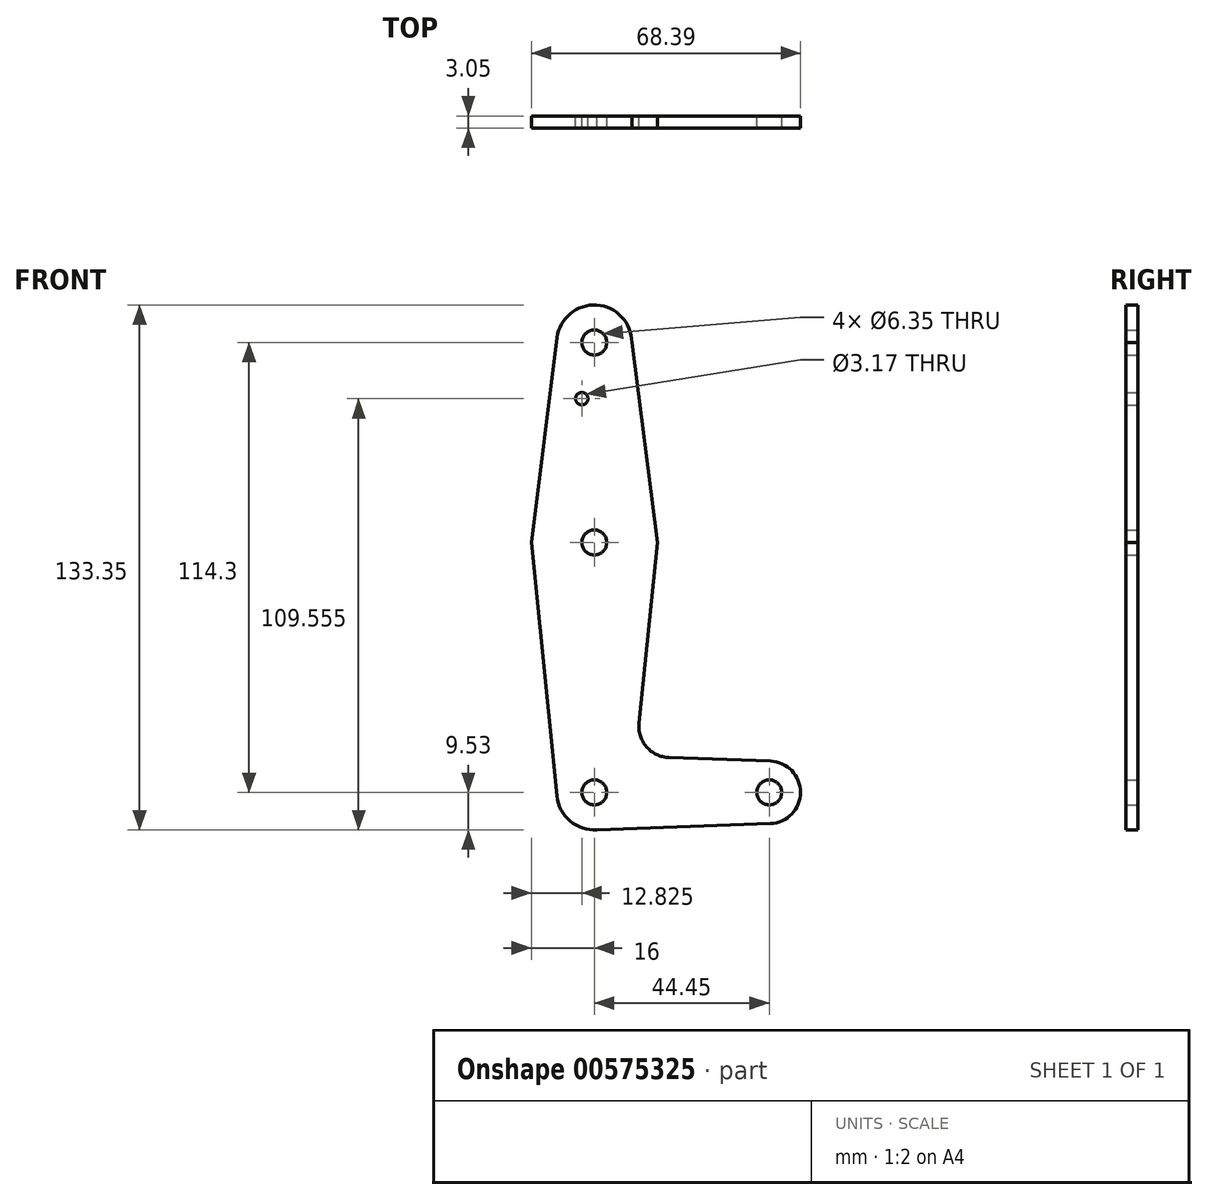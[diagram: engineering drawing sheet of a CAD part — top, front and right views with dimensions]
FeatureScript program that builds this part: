
annotation { "Feature Type Name" : "Feature", "Feature Type Description" : "" }
export const myFeature = defineFeature(function(context is Context, id is Id, definition is map)
    precondition{}
    {
        {
            var Q0;
            Q0=qCreatedBy(makeId("Front.planeOp"),FACE);
            var sketch = newSketch(context, id + "F0", { "sketchPlane" : qUnion([Q0])});
            skCircle(sketch, "E0", {"center": v(0, 0) * mm, "radius": 15.88 * mm});
            skLineSegment(sketch, "E1", {"start": v(0, 0) * mm, "end": v(0, -63.5) * mm, "construction": true});
            skCircle(sketch, "E2", {"center": v(0, -63.5) * mm, "radius": 9.53 * mm});
            skCircle(sketch, "E3", {"center": v(0, 50.8) * mm, "radius": 9.53 * mm});
            skLineSegment(sketch, "E4", {"start": v(0, -63.5) * mm, "end": v(44.45, -63.5) * mm, "construction": true});
            skCircle(sketch, "E5", {"center": v(44.45, -63.5) * mm, "radius": 7.94 * mm});
            skLineSegment(sketch, "E6", {"start": v(-9.45, 52) * mm, "end": v(-16, 0) * mm});
            skLineSegment(sketch, "E7", {"start": v(9.52, 50.8) * mm, "end": v(16, 0) * mm});
            skLineSegment(sketch, "E8", {"start": v(-16, 0) * mm, "end": v(-9.48, -64.46) * mm});
            skLineSegment(sketch, "E9", {"start": v(16, 0) * mm, "end": v(11.36, -45.9) * mm});
            skCircle(sketch, "E10", {"center": v(0, 50.8) * mm, "radius": 3.18 * mm});
            skCircle(sketch, "E11", {"center": v(0, 0) * mm, "radius": 3.18 * mm});
            skCircle(sketch, "E12", {"center": v(0, -63.5) * mm, "radius": 3.18 * mm});
            skCircle(sketch, "E13", {"center": v(44.45, -63.5) * mm, "radius": 3.18 * mm});
            skLineSegment(sketch, "E14", {"start": v(18.98, -54.65) * mm, "end": v(44.73, -55.57) * mm});
            skArc(sketch, "E15.filletArc", {"start": v(11.36, -45.9) * mm, "mid": v(13.27, -51.93) * mm, "end": v(18.98, -54.65) * mm});
            skLineSegment(sketch, "E16", {"start": v(0, 0) * mm, "end": v(0, 36.53) * mm, "construction": true});
            skLineSegment(sketch, "E17", {"start": v(0, 36.53) * mm, "end": v(-3.18, 36.53) * mm});
            skCircle(sketch, "E18", {"center": v(-3.18, 36.53) * mm, "radius": 1.59 * mm});
            skLineSegment(sketch, "E19", {"start": v(0, -73.03) * mm, "end": v(44.73, -71.43) * mm});
            skSolve(sketch);
        }
        {
            var Q0;
            Q0 = qSketchRegion(id + "F0", true);
            extrude(context, id + "F1", {"entities" : qUnion([Q0]), "depth" : 3.05 * mm, "offsetDistance" : 25.4 * mm});
        }
    });
